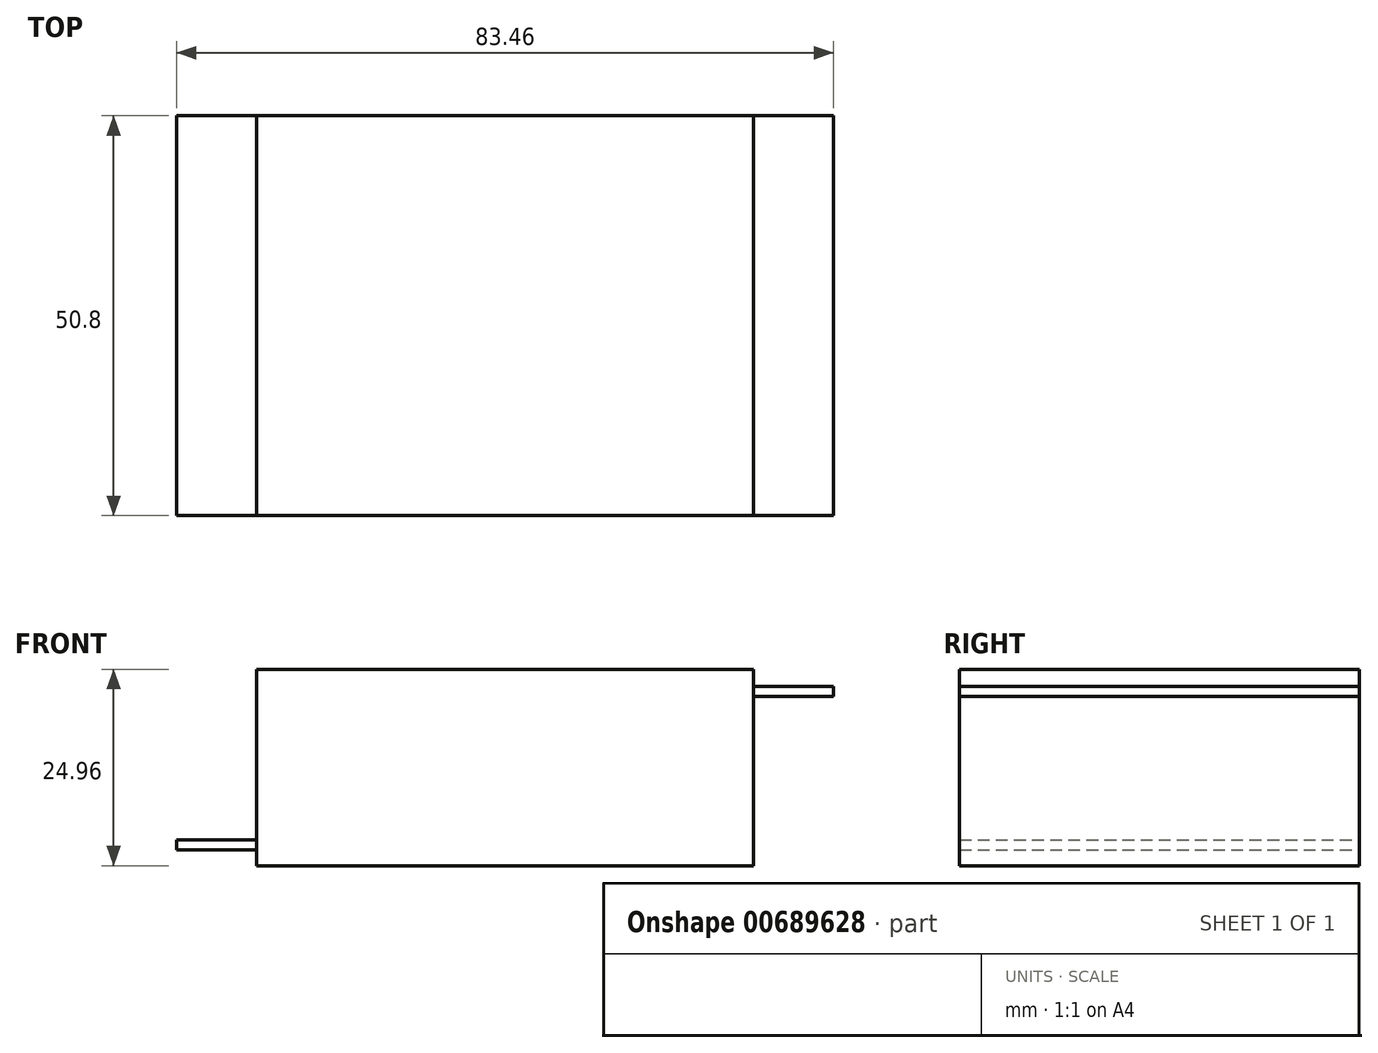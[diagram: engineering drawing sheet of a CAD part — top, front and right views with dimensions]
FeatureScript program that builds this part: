
annotation { "Feature Type Name" : "Feature", "Feature Type Description" : "" }
export const myFeature = defineFeature(function(context is Context, id is Id, definition is map)
    precondition{}
    {
        {
            var Q0;
            Q0=qCreatedBy(makeId("Front.planeOp"),FACE);
            var sketch = newSketch(context, id + "F0", { "sketchPlane" : qUnion([Q0])});
            skLineSegment(sketch, "E0.bottom", {"start": v(-31.57, 12.48) * mm, "end": v(31.57, 12.48) * mm});
            skLineSegment(sketch, "E0.top", {"start": v(-31.57, -12.48) * mm, "end": v(31.57, -12.48) * mm});
            skLineSegment(sketch, "E0.left", {"start": v(-31.57, 12.48) * mm, "end": v(-31.57, -12.48) * mm});
            skLineSegment(sketch, "E0.right", {"start": v(31.57, 12.48) * mm, "end": v(31.57, -12.48) * mm});
            skPoint(sketch, "E0.middle", {"position": v(0, 0) * mm});
            skSolve(sketch);
        }
        {
            var Q0;
            Q0=qCreatedBy(makeId("Front.planeOp"),FACE);
            var sketch = newSketch(context, id + "F1", { "sketchPlane" : qUnion([Q0])});
            skLineSegment(sketch, "E1.bottom", {"start": v(31.57, 10.3) * mm, "end": v(41.73, 10.3) * mm});
            skLineSegment(sketch, "E1.top", {"start": v(31.57, 9.03) * mm, "end": v(41.73, 9.03) * mm});
            skLineSegment(sketch, "E1.left", {"start": v(31.57, 10.3) * mm, "end": v(31.57, 9.03) * mm});
            skLineSegment(sketch, "E1.right", {"start": v(41.73, 10.3) * mm, "end": v(41.73, 9.03) * mm});
            skSolve(sketch);
        }
        {
            var Q0;
            Q0=qCreatedBy(makeId("Front.planeOp"),FACE);
            var sketch = newSketch(context, id + "F2", { "sketchPlane" : qUnion([Q0])});
            skLineSegment(sketch, "E2.bottom", {"start": v(-31.57, -10.47) * mm, "end": v(-41.73, -10.47) * mm});
            skLineSegment(sketch, "E2.top", {"start": v(-31.57, -9.2) * mm, "end": v(-41.73, -9.2) * mm});
            skLineSegment(sketch, "E2.left", {"start": v(-31.57, -10.47) * mm, "end": v(-31.57, -9.2) * mm});
            skLineSegment(sketch, "E2.right", {"start": v(-41.73, -10.47) * mm, "end": v(-41.73, -9.2) * mm});
            skSolve(sketch);
        }
        {
            var Q0;
            Q0=makeQuery(id+"F0.imprint","IMPRINT",FACE,{"disambiguationData":[TD([[makeQuery(id+"F0.imprint","IMPRINT",EDGE,{"derivedFrom":sQuery(id+"F0.wireOp",EDGE,"E0.bottom")}),-1.0]])]});
            var Q1;
            Q1=makeQuery(id+"F1.imprint","IMPRINT",FACE,{"disambiguationData":[TD([[makeQuery(id+"F1.imprint","IMPRINT",EDGE,{"derivedFrom":sQuery(id+"F1.wireOp",EDGE,"E1.bottom")}),-1.0]])]});
            var Q2;
            Q2=makeQuery(id+"F2.imprint","IMPRINT",FACE,{"disambiguationData":[TD([[makeQuery(id+"F2.imprint","IMPRINT",EDGE,{"derivedFrom":sQuery(id+"F2.wireOp",EDGE,"E2.bottom")}),-1.0]])]});
            extrude(context, id + "F3", {"entities" : qUnion([Q0, Q1, Q2]), "endBound" : BoundingType.SYMMETRIC, "depth" : 50.8 * mm, "offsetDistance" : 25.4 * mm});
        }
    });
